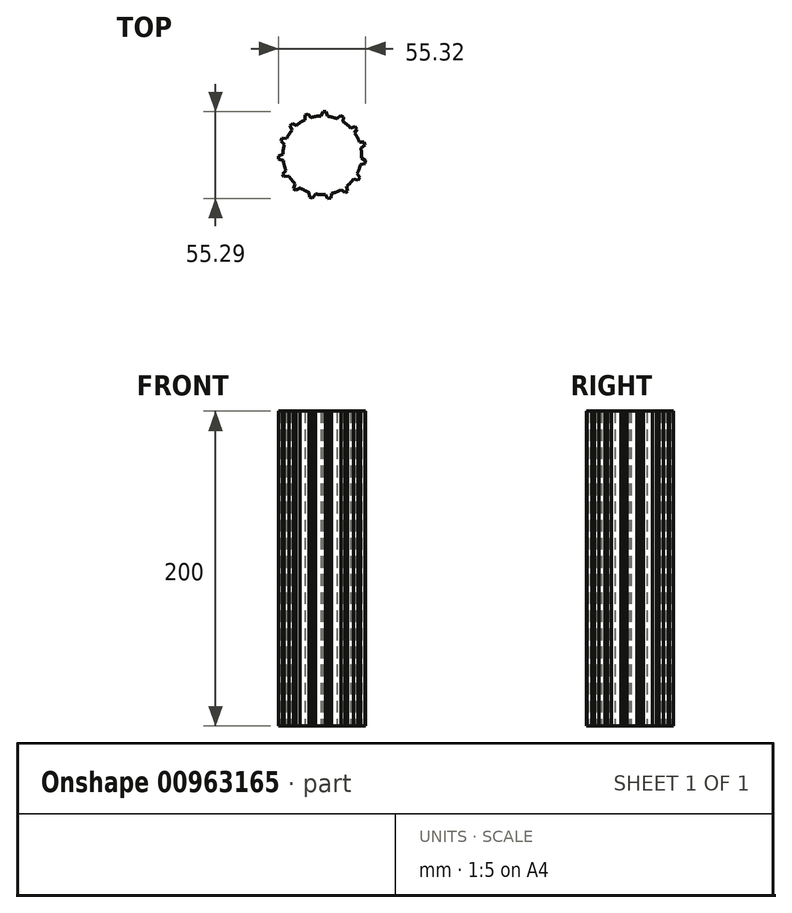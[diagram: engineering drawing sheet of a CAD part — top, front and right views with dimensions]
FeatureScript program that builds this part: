
annotation { "Feature Type Name" : "Feature", "Feature Type Description" : "" }
export const myFeature = defineFeature(function(context is Context, id is Id, definition is map)
    precondition{}
    {
        {
            var Q0;
            Q0=qCreatedBy(makeId("Top.planeOp"),FACE);
            var sketch = newSketch(context, id + "F0", { "sketchPlane" : qUnion([Q0])});
            skCircle(sketch, "E0", {"center": v(0, 0) * mm, "radius": 25 * mm});
            skLineSegment(sketch, "E1", {"start": v(23.5, 8.51) * mm, "end": v(26.5, 8.26) * mm});
            skLineSegment(sketch, "E2", {"start": v(26.5, 8.26) * mm, "end": v(27.02, 6.33) * mm});
            skLineSegment(sketch, "E3", {"start": v(27.02, 6.33) * mm, "end": v(24.57, 4.6) * mm});
            skLineSegment(sketch, "E4.1.0", {"start": v(18.01, 17.34) * mm, "end": v(20.84, 18.33) * mm});
            skLineSegment(sketch, "E4.1.1", {"start": v(20.84, 18.33) * mm, "end": v(22.11, 16.78) * mm});
            skLineSegment(sketch, "E4.1.2", {"start": v(22.11, 16.78) * mm, "end": v(20.58, 14.2) * mm});
            skLineSegment(sketch, "E4.2.0", {"start": v(9.4, 23.16) * mm, "end": v(11.59, 25.22) * mm});
            skLineSegment(sketch, "E4.2.1", {"start": v(11.59, 25.22) * mm, "end": v(13.37, 24.32) * mm});
            skLineSegment(sketch, "E4.2.2", {"start": v(13.37, 24.32) * mm, "end": v(13.02, 21.34) * mm});
            skLineSegment(sketch, "E4.3.0", {"start": v(-0.83, 24.99) * mm, "end": v(0.33, 27.75) * mm});
            skLineSegment(sketch, "E4.3.1", {"start": v(0.33, 27.75) * mm, "end": v(2.33, 27.66) * mm});
            skLineSegment(sketch, "E4.3.2", {"start": v(2.33, 27.66) * mm, "end": v(3.22, 24.8) * mm});
            skLineSegment(sketch, "E4.4.0", {"start": v(-10.92, 22.49) * mm, "end": v(-10.99, 25.49) * mm});
            skLineSegment(sketch, "E4.4.1", {"start": v(-10.99, 25.49) * mm, "end": v(-9.12, 26.21) * mm});
            skLineSegment(sketch, "E4.4.2", {"start": v(-9.12, 26.21) * mm, "end": v(-7.15, 23.96) * mm});
            skLineSegment(sketch, "E4.5.0", {"start": v(-19.12, 16.1) * mm, "end": v(-20.4, 18.82) * mm});
            skLineSegment(sketch, "E4.5.1", {"start": v(-20.4, 18.82) * mm, "end": v(-19, 20.24) * mm});
            skLineSegment(sketch, "E4.5.2", {"start": v(-19, 20.24) * mm, "end": v(-16.27, 18.98) * mm});
            skLineSegment(sketch, "E4.6.0", {"start": v(-24.02, 6.93) * mm, "end": v(-26.3, 8.89) * mm});
            skLineSegment(sketch, "E4.6.1", {"start": v(-26.3, 8.89) * mm, "end": v(-25.58, 10.76) * mm});
            skLineSegment(sketch, "E4.6.2", {"start": v(-25.58, 10.76) * mm, "end": v(-22.58, 10.72) * mm});
            skLineSegment(sketch, "E4.7.0", {"start": v(-24.76, -3.44) * mm, "end": v(-27.64, -2.57) * mm});
            skLineSegment(sketch, "E4.7.1", {"start": v(-27.64, -2.57) * mm, "end": v(-27.75, -0.58) * mm});
            skLineSegment(sketch, "E4.7.2", {"start": v(-27.75, -0.58) * mm, "end": v(-25, 0.6) * mm});
            skLineSegment(sketch, "E4.8.0", {"start": v(-21.22, -13.21) * mm, "end": v(-24.2, -13.6) * mm});
            skLineSegment(sketch, "E4.8.1", {"start": v(-24.2, -13.6) * mm, "end": v(-25.12, -11.81) * mm});
            skLineSegment(sketch, "E4.8.2", {"start": v(-25.12, -11.81) * mm, "end": v(-23.08, -9.61) * mm});
            skLineSegment(sketch, "E4.9.0", {"start": v(-14.01, -20.7) * mm, "end": v(-16.58, -22.26) * mm});
            skLineSegment(sketch, "E4.9.1", {"start": v(-16.58, -22.26) * mm, "end": v(-18.14, -21) * mm});
            skLineSegment(sketch, "E4.9.2", {"start": v(-18.14, -21) * mm, "end": v(-17.17, -18.17) * mm});
            skLineSegment(sketch, "E4.10.0", {"start": v(-4.38, -24.61) * mm, "end": v(-6.1, -27.08) * mm});
            skLineSegment(sketch, "E4.10.1", {"start": v(-6.1, -27.08) * mm, "end": v(-8.03, -26.57) * mm});
            skLineSegment(sketch, "E4.10.2", {"start": v(-8.03, -26.57) * mm, "end": v(-8.3, -23.58) * mm});
            skLineSegment(sketch, "E4.11.0", {"start": v(6, -24.27) * mm, "end": v(5.45, -27.21) * mm});
            skLineSegment(sketch, "E4.11.1", {"start": v(5.45, -27.21) * mm, "end": v(3.47, -27.54) * mm});
            skLineSegment(sketch, "E4.11.2", {"start": v(3.47, -27.54) * mm, "end": v(2, -24.92) * mm});
            skLineSegment(sketch, "E4.12.0", {"start": v(15.36, -19.73) * mm, "end": v(16.05, -22.65) * mm});
            skLineSegment(sketch, "E4.12.1", {"start": v(16.05, -22.65) * mm, "end": v(14.37, -23.74) * mm});
            skLineSegment(sketch, "E4.12.2", {"start": v(14.37, -23.74) * mm, "end": v(11.97, -21.95) * mm});
            skLineSegment(sketch, "E4.13.0", {"start": v(22.05, -11.77) * mm, "end": v(23.87, -14.16) * mm});
            skLineSegment(sketch, "E4.13.1", {"start": v(23.87, -14.16) * mm, "end": v(22.79, -15.84) * mm});
            skLineSegment(sketch, "E4.13.2", {"start": v(22.79, -15.84) * mm, "end": v(19.86, -15.18) * mm});
            skLineSegment(sketch, "E4.14.0", {"start": v(24.94, -1.79) * mm, "end": v(27.57, -3.23) * mm});
            skLineSegment(sketch, "E4.14.1", {"start": v(27.57, -3.23) * mm, "end": v(27.26, -5.2) * mm});
            skLineSegment(sketch, "E4.14.2", {"start": v(27.26, -5.2) * mm, "end": v(24.32, -5.8) * mm});
            skSolve(sketch);
        }
        {
            var Q0;
            {var subQ0=sQuery(id+"F0.wireOp",EDGE,"E0");var subQ17=makeQuery(id+"F0.imprint","INTERSECT",VERTEX,{"derivedFrom":[subQ0,sQuery(id+"F0.wireOp",EDGE,"E1")]});Q0=makeQuery(id+"F0.imprint","IMPRINT",FACE,{"disambiguationData":[TD([[makeQuery(id+"F0.imprint","IMPRINT",EDGE,{"disambiguationData":[TD([[subQ17,1.0]])],"derivedFrom":subQ0}),1.0]])]});}
            var Q1;
            {var subQ0=sQuery(id+"F0.wireOp",EDGE,"E4.7.0");Q1=makeQuery(id+"F0.imprint","IMPRINT",FACE,{"disambiguationData":[TD([[makeQuery(id+"F0.imprint","IMPRINT",EDGE,{"derivedFrom":subQ0}),-1.0]])]});}
            var Q2;
            {var subQ0=sQuery(id+"F0.wireOp",EDGE,"E1");Q2=makeQuery(id+"F0.imprint","IMPRINT",FACE,{"disambiguationData":[TD([[makeQuery(id+"F0.imprint","IMPRINT",EDGE,{"derivedFrom":subQ0}),-1.0]])]});}
            var Q3;
            {var subQ0=sQuery(id+"F0.wireOp",EDGE,"E4.1.0");Q3=makeQuery(id+"F0.imprint","IMPRINT",FACE,{"disambiguationData":[TD([[makeQuery(id+"F0.imprint","IMPRINT",EDGE,{"derivedFrom":subQ0}),-1.0]])]});}
            var Q4;
            {var subQ0=sQuery(id+"F0.wireOp",EDGE,"E4.2.0");Q4=makeQuery(id+"F0.imprint","IMPRINT",FACE,{"disambiguationData":[TD([[makeQuery(id+"F0.imprint","IMPRINT",EDGE,{"derivedFrom":subQ0}),-1.0]])]});}
            var Q5;
            {var subQ0=sQuery(id+"F0.wireOp",EDGE,"E4.3.0");Q5=makeQuery(id+"F0.imprint","IMPRINT",FACE,{"disambiguationData":[TD([[makeQuery(id+"F0.imprint","IMPRINT",EDGE,{"derivedFrom":subQ0}),-1.0]])]});}
            var Q6;
            {var subQ0=sQuery(id+"F0.wireOp",EDGE,"E4.4.0");Q6=makeQuery(id+"F0.imprint","IMPRINT",FACE,{"disambiguationData":[TD([[makeQuery(id+"F0.imprint","IMPRINT",EDGE,{"derivedFrom":subQ0}),-1.0]])]});}
            var Q7;
            {var subQ0=sQuery(id+"F0.wireOp",EDGE,"E4.5.0");Q7=makeQuery(id+"F0.imprint","IMPRINT",FACE,{"disambiguationData":[TD([[makeQuery(id+"F0.imprint","IMPRINT",EDGE,{"derivedFrom":subQ0}),-1.0]])]});}
            var Q8;
            {var subQ0=sQuery(id+"F0.wireOp",EDGE,"E4.12.0");Q8=makeQuery(id+"F0.imprint","IMPRINT",FACE,{"disambiguationData":[TD([[makeQuery(id+"F0.imprint","IMPRINT",EDGE,{"derivedFrom":subQ0}),-1.0]])]});}
            var Q9;
            {var subQ0=sQuery(id+"F0.wireOp",EDGE,"E4.13.0");Q9=makeQuery(id+"F0.imprint","IMPRINT",FACE,{"disambiguationData":[TD([[makeQuery(id+"F0.imprint","IMPRINT",EDGE,{"derivedFrom":subQ0}),-1.0]])]});}
            var Q10;
            {var subQ0=sQuery(id+"F0.wireOp",EDGE,"E4.14.0");Q10=makeQuery(id+"F0.imprint","IMPRINT",FACE,{"disambiguationData":[TD([[makeQuery(id+"F0.imprint","IMPRINT",EDGE,{"derivedFrom":subQ0}),-1.0]])]});}
            var Q11;
            {var subQ0=sQuery(id+"F0.wireOp",EDGE,"E4.11.0");Q11=makeQuery(id+"F0.imprint","IMPRINT",FACE,{"disambiguationData":[TD([[makeQuery(id+"F0.imprint","IMPRINT",EDGE,{"derivedFrom":subQ0}),-1.0]])]});}
            var Q12;
            {var subQ0=sQuery(id+"F0.wireOp",EDGE,"E4.10.0");Q12=makeQuery(id+"F0.imprint","IMPRINT",FACE,{"disambiguationData":[TD([[makeQuery(id+"F0.imprint","IMPRINT",EDGE,{"derivedFrom":subQ0}),-1.0]])]});}
            var Q13;
            {var subQ0=sQuery(id+"F0.wireOp",EDGE,"E4.9.0");Q13=makeQuery(id+"F0.imprint","IMPRINT",FACE,{"disambiguationData":[TD([[makeQuery(id+"F0.imprint","IMPRINT",EDGE,{"derivedFrom":subQ0}),-1.0]])]});}
            var Q14;
            {var subQ0=sQuery(id+"F0.wireOp",EDGE,"E4.8.0");Q14=makeQuery(id+"F0.imprint","IMPRINT",FACE,{"disambiguationData":[TD([[makeQuery(id+"F0.imprint","IMPRINT",EDGE,{"derivedFrom":subQ0}),-1.0]])]});}
            var Q15;
            {var subQ0=sQuery(id+"F0.wireOp",EDGE,"E4.6.0");Q15=makeQuery(id+"F0.imprint","IMPRINT",FACE,{"disambiguationData":[TD([[makeQuery(id+"F0.imprint","IMPRINT",EDGE,{"derivedFrom":subQ0}),-1.0]])]});}
            extrude(context, id + "F1", {"entities" : qUnion([Q0, Q1, Q2, Q3, Q4, Q5, Q6, Q7, Q8, Q9, Q10, Q11, Q12, Q13, Q14, Q15]), "depth" : 200 * mm, "offsetDistance" : 25 * mm});
        }
    });
